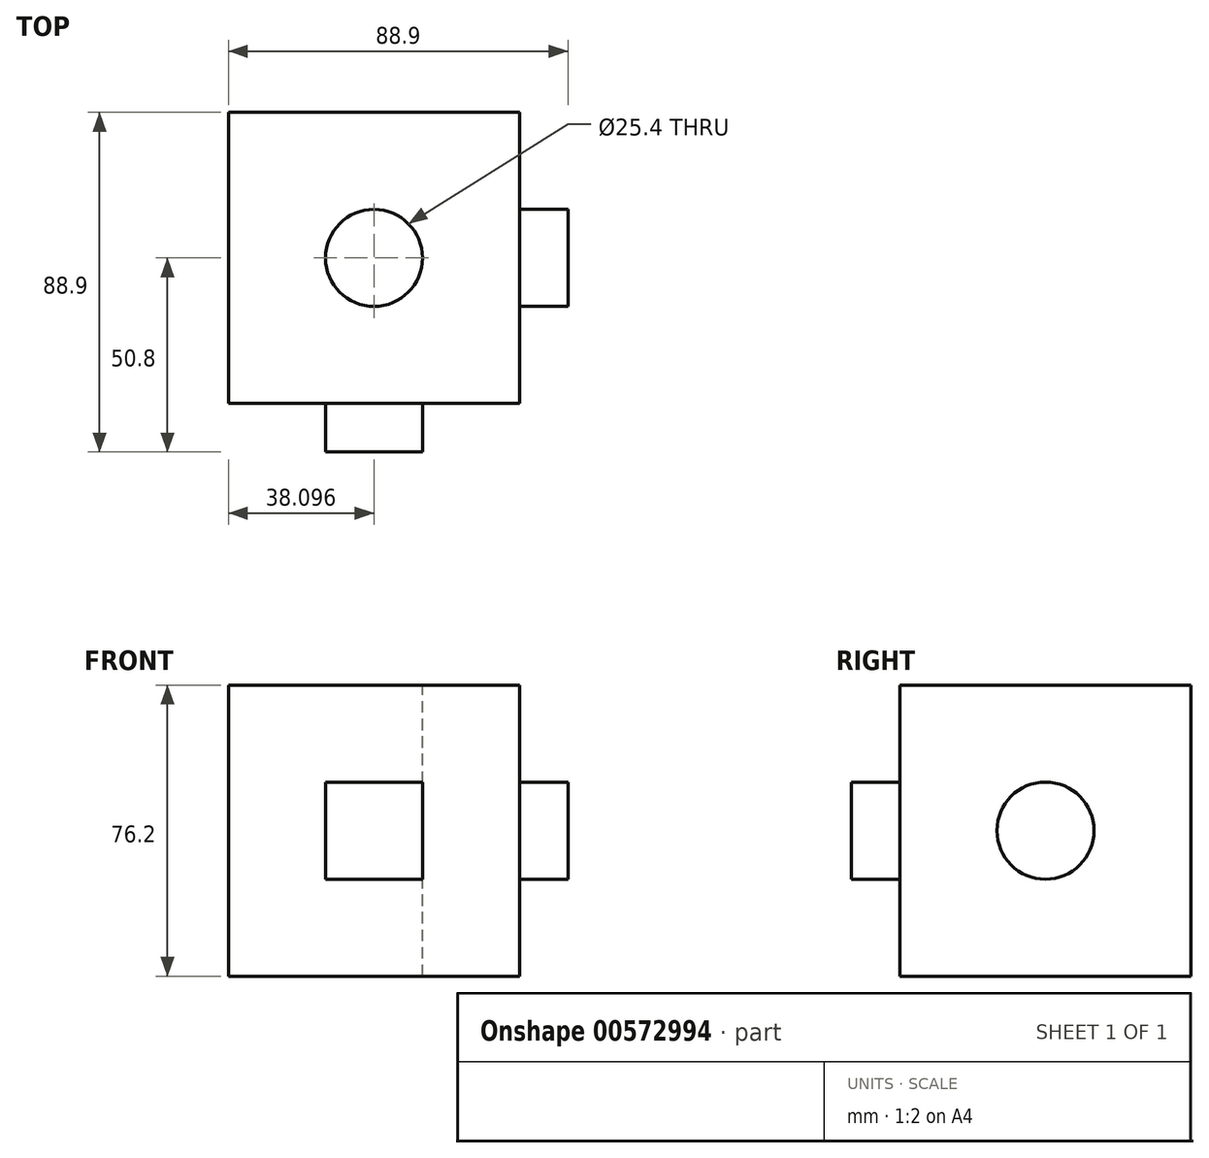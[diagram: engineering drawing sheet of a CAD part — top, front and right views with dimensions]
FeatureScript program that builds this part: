
annotation { "Feature Type Name" : "Feature", "Feature Type Description" : "" }
export const myFeature = defineFeature(function(context is Context, id is Id, definition is map)
    precondition{}
    {
        {
            var Q0;
            Q0=qCreatedBy(makeId("Front.planeOp"),FACE);
            var sketch = newSketch(context, id + "F0", { "sketchPlane" : qUnion([Q0])});
            skLineSegment(sketch, "E0.bottom", {"start": v(-73.52, 68.22) * mm, "end": v(2.68, 68.22) * mm});
            skLineSegment(sketch, "E0.top", {"start": v(-73.52, -7.98) * mm, "end": v(2.68, -7.98) * mm});
            skLineSegment(sketch, "E0.left", {"start": v(-73.52, 68.22) * mm, "end": v(-73.52, -7.98) * mm});
            skLineSegment(sketch, "E0.right", {"start": v(2.68, 68.22) * mm, "end": v(2.68, -7.98) * mm});
            skSolve(sketch);
        }
        {
            var Q0;
            Q0=makeQuery(id+"F0.imprint","IMPRINT",FACE,{"disambiguationData":[TD([[makeQuery(id+"F0.imprint","IMPRINT",EDGE,{"derivedFrom":sQuery(id+"F0.wireOp",EDGE,"E0.bottom")}),-1.0]])]});
            extrude(context, id + "F1", {"entities" : qUnion([Q0]), "depth" : 76.2 * mm, "offsetDistance" : 25.4 * mm});
        }
        {
            var Q0;
            Q0=makeQuery(id+"F1.opExtrude","CAP_FACE",FACE,{"disambiguationData":[OSD([sQuery(id+"F0.wireOp",EDGE,"E0.bottom"),sQuery(id+"F0.wireOp",EDGE,"E0.top"),sQuery(id+"F0.wireOp",EDGE,"E0.left"),sQuery(id+"F0.wireOp",EDGE,"E0.right")])],"isStart":false});
            var sketch = newSketch(context, id + "F2", { "sketchPlane" : qUnion([Q0])});
            skLineSegment(sketch, "E1.bottom", {"start": v(-48.12, 42.82) * mm, "end": v(-22.72, 42.82) * mm});
            skLineSegment(sketch, "E1.top", {"start": v(-48.12, 17.42) * mm, "end": v(-22.72, 17.42) * mm});
            skLineSegment(sketch, "E1.left", {"start": v(-48.12, 42.82) * mm, "end": v(-48.12, 17.42) * mm});
            skLineSegment(sketch, "E1.right", {"start": v(-22.72, 42.82) * mm, "end": v(-22.72, 17.42) * mm});
            skSolve(sketch);
        }
        {
            var Q0;
            Q0=makeQuery(id+"F2.imprint","IMPRINT",FACE,{"disambiguationData":[TD([[makeQuery(id+"F2.imprint","IMPRINT",EDGE,{"derivedFrom":sQuery(id+"F2.wireOp",EDGE,"E1.bottom")}),-1.0]])]});
            extrude(context, id + "F3", {"entities" : qUnion([Q0]), "operationType" : NewBodyOperationType.ADD, "depth" : 12.7 * mm, "offsetDistance" : 25.4 * mm});
        }
        {
            var Q0;
            Q0=makeQuery(id+"F1.opExtrude","SWEPT_FACE",FACE,{"disambiguationData":[OSD([sQuery(id+"F0.wireOp",EDGE,"E0.right")])]});
            var sketch = newSketch(context, id + "F4", { "sketchPlane" : qUnion([Q0])});
            skCircle(sketch, "E2", {"center": v(-38.1, 30.12) * mm, "radius": 12.7 * mm});
            skSolve(sketch);
        }
        {
            var Q0;
            Q0=makeQuery(id+"F4.imprint","IMPRINT",FACE,{"disambiguationData":[TD([[makeQuery(id+"F4.imprint","IMPRINT",EDGE,{"derivedFrom":sQuery(id+"F4.wireOp",EDGE,"E2")}),1.0]])]});
            extrude(context, id + "F5", {"entities" : qUnion([Q0]), "operationType" : NewBodyOperationType.ADD, "depth" : 12.7 * mm, "offsetDistance" : 25.4 * mm});
        }
        {
            var Q0;
            Q0=makeQuery(id+"F1.opExtrude","SWEPT_FACE",FACE,{"disambiguationData":[OSD([sQuery(id+"F0.wireOp",EDGE,"E0.bottom")])]});
            var sketch = newSketch(context, id + "F6", { "sketchPlane" : qUnion([Q0])});
            skPoint(sketch, "E3", {"position": v(-35.42, -38.1) * mm});
            skSolve(sketch);
        }
        {
            var Q0;
            Q0=sQuery(id+"F6.wireOp",VERTEX,"E3");
            var Q1;
            Q1=makeQuery(id+"F1.opExtrude","SWEPT_BODY",BODY,{"disambiguationData":[OSD([sQuery(id+"F0.wireOp",EDGE,"E0.bottom"),sQuery(id+"F0.wireOp",EDGE,"E0.top"),sQuery(id+"F0.wireOp",EDGE,"E0.left"),sQuery(id+"F0.wireOp",EDGE,"E0.right")])]});
            hole(context, id + "F7", {"style" : HoleStyle.SIMPLE, "endStyle" : HoleEndStyle.THROUGH, "holeDiameter" : 25.4 * mm, "isTappedThrough" : true, "tappedDepth" : 12.7 * mm, "tapClearance" : 3, "locations" : qUnion([Q0]), "scope" : qUnion([Q1])});
        }
    });
